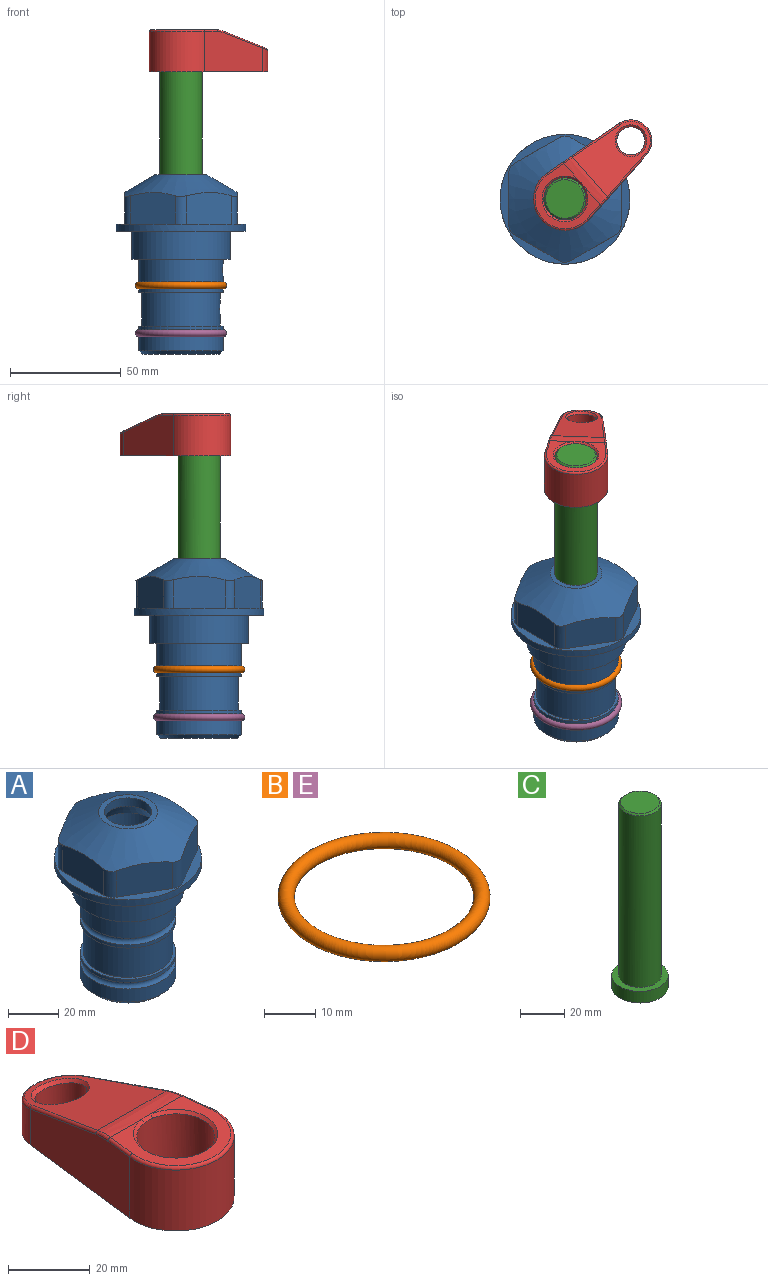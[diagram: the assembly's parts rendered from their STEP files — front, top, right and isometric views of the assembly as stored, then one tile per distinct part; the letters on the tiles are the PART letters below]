
ASSEMBLY  parts=5 mates=3
PART A: 36 faces, bbox 58.7x58.7x81 mm
  f0: cylinder r=17.78mm len=35.56mm, axis (0,0,1), area 1670.8mm2, adj f23,f24,f31
  f1: cylinder r=19.05mm len=38.1mm, axis (0,0,1), area 1191.9mm2, adj f26,f27,f30
  f2: plane 58.66x58.66mm, normal (0,0,-1), area 1150.6mm2, adj f3,f28
  f3: cylinder r=29.33mm len=58.66mm, axis (0,0,-1), area 585.1mm2, adj f2,f4
  f4: plane 58.66x58.66mm, normal (0,0,1), area 475.9mm2, adj f3,f5,f6,f7,f8,f9,f10,f11
  f5: plane 20.32x14.34mm, normal (-0.5,0.87,0), area 324.4mm2, adj f4,f15,f16,f17
  f6: plane 20.32x14.34mm, normal (0.5,0.87,0), area 324.4mm2, adj f4,f14,f15,f17
  f7: plane 23.48x14.34mm, normal (1,0,0), area 324.4mm2, adj f4,f13,f14,f17
  f8: plane 20.32x14.34mm, normal (0.5,-0.87,0), area 324.4mm2, adj f4,f12,f13,f17
  f9: plane 20.32x14.34mm, normal (-0.5,-0.87,0), area 324.4mm2, adj f4,f11,f12,f17
  f10: plane 23.48x14.34mm, normal (-1,0,0), area 324.4mm2, adj f4,f11,f16,f17
  f11: cylinder r=5.08mm len=12.85mm, axis (0,0,-1), area 67.2mm2, adj f4,f9,f10,f17
  f12: cylinder r=5.08mm len=12.85mm, axis (0,0,-1), area 67.2mm2, adj f4,f8,f9,f17
  f13: cylinder r=5.08mm len=12.85mm, axis (0,0,-1), area 67.2mm2, adj f4,f7,f8,f17
  f14: cylinder r=5.08mm len=12.85mm, axis (0,0,-1), area 67.2mm2, adj f4,f6,f7,f17
  f15: cylinder r=5.08mm len=12.85mm, axis (0,0,-1), area 67.2mm2, adj f4,f5,f6,f17
  f16: cylinder r=5.08mm len=12.85mm, axis (0,0,-1), area 67.2mm2, adj f4,f5,f10,f17
  f17: cone r=11.73mm half-angle=60deg, axis (0,0,-1), area 2071.8mm2, adj f5,f6,f7,f8,f9,f10,f11,f12
  f18: plane 23.46x23.46mm, normal (0,0,1), area 147.4mm2, adj f17,f35
  f19: plane 34.93x34.93mm, normal (0,0,-1), area 958mm2, adj f29
  f20: cylinder r=19.05mm len=38.1mm, axis (0,0,1), area 760.1mm2, adj f21,f29
  f21: torus R=19.05mm, axis (0,0,1), area 565.3mm2, adj f20,f22
  f22: cylinder r=19.05mm len=38.1mm, axis (0,0,1), area 190mm2, adj f21,f23
  f23: plane 38.1x38.1mm, normal (0,0,1), area 146.9mm2, adj f0,f22
  f24: plane 38.1x38.1mm, normal (0,0,-1), area 146.9mm2, adj f0,f25
  f25: cylinder r=19.05mm len=38.1mm, axis (0,0,1), area 190mm2, adj f24,f26
  f26: torus R=19.05mm, axis (0,0,1), area 565.3mm2, adj f1,f25
  f27: plane 44.45x44.45mm, normal (0,0,-1), area 411.7mm2, adj f1,f28
  f28: cylinder r=22.23mm len=44.45mm, axis (0,0,1), area 1773.5mm2, adj f2,f27
  f29: cone r=19.05mm half-angle=45deg, axis (0,0,1), area 257.5mm2, adj f19,f20
  f30: cylinder r=3.17mm len=6.75mm, axis (-1,0,0), area 128mm2, adj f1,f33
  f31: cylinder r=3.17mm len=6.35mm, axis (-1,0,0), area 102.5mm2, adj f0,f33
  f32: plane 25.4x25.4mm, normal (0,0,1), area 506.7mm2, adj f33
  f33: cylinder r=12.7mm len=66.42mm, axis (0,0,-1), area 5236.2mm2, adj f30,f31,f32,f34
  f34: cone r=9.53mm half-angle=30deg, axis (0,0,-1), area 443.4mm2, adj f33,f35
  f35: cylinder r=9.53mm len=19.05mm, axis (0,0,-1), area 240.9mm2, adj f18,f34
PART B: 1 faces, bbox 44.7x44.7x3.2 mm
  f0: torus R=19.05mm, axis (0,0,1), area 1193.9mm2
PART C: 6 faces, bbox 25.4x25.4x101.6 mm
  f0: plane 17.46x17.46mm, normal (0,0,1), area 239.5mm2, adj f5
  f1: plane 25.4x25.4mm, normal (0,0,-1), area 506.7mm2, adj f2
  f2: cylinder r=12.7mm len=25.4mm, axis (0,0,1), area 506.7mm2, adj f1,f3
  f3: plane 25.4x25.4mm, normal (0,0,1), area 221.7mm2, adj f2,f4
  f4: cylinder r=9.53mm len=94.46mm, axis (0,0,1), area 5653mm2, adj f3,f5
  f5: cone r=8.73mm half-angle=45deg, axis (0,0,-1), area 64.4mm2, adj f0,f4
PART D: 31 faces, bbox 31.7x65.5x19.8 mm
  f0: plane 39.12x18.26mm, normal (0.99,0.12,0), area 612.2mm2, adj f1,f4,f7,f11,f13,f15
  f1: cylinder r=9.53mm len=18.91mm, axis (0,0,-1), area 296.1mm2, adj f0,f2,f7,f17
  f2: plane 39.12x18.26mm, normal (-0.99,0.12,0), area 612.2mm2, adj f1,f4,f7,f12,f14,f16
  f3: cylinder r=6.35mm len=12.7mm, axis (0,0,-1), area 362.4mm2, adj f7,f18
  f4: cylinder r=14.29mm len=28.58mm, axis (0,0,-1), area 882.2mm2, adj f0,f2,f7,f10
  f5: cylinder r=9.53mm len=19.05mm, axis (0,0,-1), area 1092.6mm2, adj f7,f19,f20
  f6: plane 26.99x23.69mm, normal (0,0,1), area 216.2mm2, adj f9,f10,f11,f12,f19
  f7: plane 63.5x28.58mm, normal (0,0,-1), area 661.8mm2, adj f0,f1,f2,f3,f4,f5,f22,f23
  f8: plane 33.52x23.6mm, normal (0,0.26,0.97), area 486mm2, adj f9,f15,f16,f17,f18
  f9: cylinder r=19.05mm len=24.72mm, axis (1,0,0), area 120.4mm2, adj f6,f8,f13,f14,f20
  f10: torus R=13.49mm, axis (0,0,1), area 59mm2, adj f4,f6,f11,f12
  f11: cylinder r=0.79mm len=8.67mm, axis (0.12,-0.99,0), area 10.8mm2, adj f0,f6,f10,f13
  f12: cylinder r=0.79mm len=8.67mm, axis (0.12,0.99,0), area 10.8mm2, adj f2,f6,f10,f14
  f13: bspline ~4.95x1.42mm, area 6.1mm2, adj f0,f9,f11,f15
  f14: bspline ~4.95x1.42mm, area 6.1mm2, adj f2,f9,f12,f16
  f15: cylinder r=0.79mm len=25.95mm, axis (0.12,-0.96,0.26), area 32.9mm2, adj f0,f8,f13,f17
  f16: cylinder r=0.79mm len=25.95mm, axis (0.12,0.96,-0.26), area 32.9mm2, adj f2,f8,f14,f17
  f17: bspline ~18.91x8.38mm, area 30mm2, adj f1,f8,f15,f16
  f18: bspline ~14.29x14.29mm, area 48.3mm2, adj f3,f8
  f19: cone r=9.53mm half-angle=45deg, axis (0,0,1), area 66.5mm2, adj f5,f6,f20
  f20: bspline ~3.22x0.96mm, area 3.5mm2, adj f5,f9,f19
  f21: plane 2.75x2.72mm, normal (0,0,-1), area 2.9mm2, adj f23,f25,f28
  f22: plane 23.05x15.88mm, normal (-0.99,-0.12,0), area 323.6mm2, adj f7,f25,f26,f27,f28,f29
  f23: plane 23.05x15.88mm, normal (0.99,-0.12,0), area 323.6mm2, adj f7,f21,f25,f27,f28,f30
  f24: cylinder r=9.53mm len=10.69mm, axis (0,0,-1), area 114.7mm2, adj f7,f27,f29,f30
  f25: cylinder r=12.7mm len=20.59mm, axis (0,0,-1), area 381.1mm2, adj f7,f21,f22,f23,f26,f28
  f26: plane 2.75x2.72mm, normal (0,0,-1), area 2.9mm2, adj f22,f25,f28
  f27: plane 19.72x18.37mm, normal (0,-0.26,-0.97), area 291.8mm2, adj f22,f23,f24,f28,f29,f30
  f28: cylinder r=15.88mm len=19.92mm, axis (1,0,0), area 54.8mm2, adj f21,f22,f23,f25,f26,f27
  f29: cylinder r=1.59mm len=11mm, axis (0,0,-1), area 34.7mm2, adj f7,f22,f24,f27
  f30: cylinder r=1.59mm len=11mm, axis (0,0,-1), area 34.7mm2, adj f7,f23,f24,f27
PART E: same geometry as B
PLACE A at identity fixed
PLACE B at identity
PLACE C rot(axis=(0,0,-1),48.6deg) t=(0,0,27.55)mm
PLACE D rot(axis=(0,0,-1),48.6deg) t=(0,0,27.55)mm
PLACE E t=(0,0,-21.59)mm
MATE fastened C.f2 <-> D.f4  axis (0,0,1) through (0,0,91.05)mm
MATE fastened E.f0 <-> A.f0  axis (0,0,1) through (0,0,-46.1)mm
MATE cylindrical C.f2 <-> A.f0  axis (0,0,-1) through (0,0,-10.55)mm
